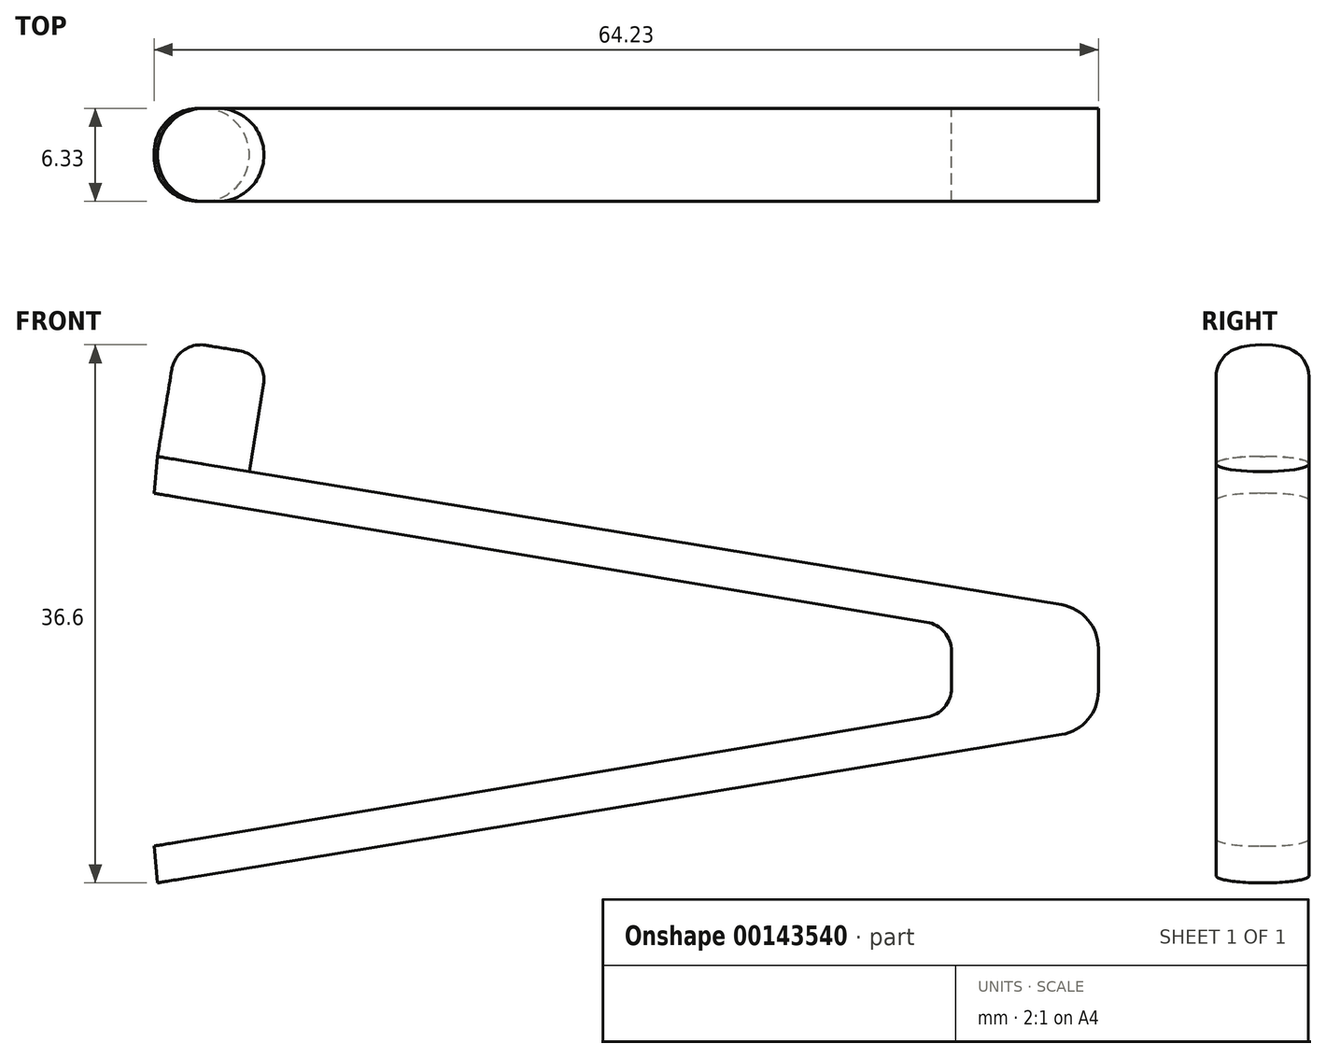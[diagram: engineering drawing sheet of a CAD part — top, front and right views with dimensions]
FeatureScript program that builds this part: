
annotation { "Feature Type Name" : "Feature", "Feature Type Description" : "" }
export const myFeature = defineFeature(function(context is Context, id is Id, definition is map)
    precondition{}
    {
        {
            var Q0;
            Q0=qCreatedBy(makeId("Front.planeOp"),FACE);
            var sketch = newSketch(context, id + "F0", { "sketchPlane" : qUnion([Q0])});
            skLineSegment(sketch, "E0", {"start": v(-30, 14.5) * mm, "end": v(34, 4) * mm});
            skLineSegment(sketch, "E1", {"start": v(34, 4) * mm, "end": v(34, -4) * mm});
            skLineSegment(sketch, "E2", {"start": v(34, -4) * mm, "end": v(-30, -14.5) * mm});
            skLineSegment(sketch, "E3.1", {"start": v(24, -2.96) * mm, "end": v(-30.23, -12) * mm});
            skLineSegment(sketch, "E3.2", {"start": v(-30.23, 12) * mm, "end": v(24, 2.96) * mm});
            skLineSegment(sketch, "E4", {"start": v(24, 2.96) * mm, "end": v(24, -2.96) * mm});
            skLineSegment(sketch, "E5", {"start": v(-30, 14.5) * mm, "end": v(-30.23, 12) * mm});
            skLineSegment(sketch, "E6", {"start": v(-30.23, -12) * mm, "end": v(-30, -14.5) * mm});
            skSolve(sketch);
        }
        {
            var Q0;
            Q0=makeQuery(id+"F0.imprint","IMPRINT",FACE,{"disambiguationData":[TD([[makeQuery(id+"F0.imprint","IMPRINT",EDGE,{"derivedFrom":sQuery(id+"F0.wireOp",EDGE,"E0")}),-1.0]])]});
            var Q1;
            Q1=sQuery(id+"F0.wireOp",EDGE,"9byXGtGL-TiKi-ESHT-9G8f-rp2WdieyN90J");
            var Q2;
            Q2=sQuery(id+"F0.wireOp",EDGE,"E1");
            var Q3;
            Q3=sQuery(id+"F0.wireOp",EDGE,"E3.0");
            var Q4;
            Q4=sQuery(id+"F0.wireOp",EDGE,"E2");
            var Q5;
            Q5=sQuery(id+"F0.wireOp",EDGE,"E3.1");
            var Q6;
            Q6=sQuery(id+"F0.wireOp",EDGE,"E3.2");
            var Q7;
            Q7=sQuery(id+"F0.wireOp",EDGE,"E3.3");
            var Q8;
            Q8=sQuery(id+"F0.wireOp",EDGE,"E0");
            var Q9;
            Q9=sQuery(id+"F0.wireOp",EDGE,"E4");
            var Q10;
            Q10=sQuery(id+"F0.wireOp",EDGE,"WK7Iqi4k-UJnr-hG7o-36dU-zjlxEIJufRnm");
            var Q11;
            Q11=sQuery(id+"F0.wireOp",EDGE,"wQO7SIwi-us3T-ShAA-4KbL-jPIoXWtiWfxA");
            var Q12;
            Q12=sQuery(id+"F0.wireOp",EDGE,"2IcxQzrb-WH7L-S9HZ-jIrS-pt4sDyhrxdYz");
            extrude(context, id + "F1", {"entities" : qUnion([Q0]), "surfaceEntities" : qUnion([Q1, Q2, Q3, Q4, Q5, Q6, Q7, Q8, Q9, Q10, Q11, Q12]), "depth" : 6.33 * mm});
        }
        {
            var Q0;
            Q0=makeQuery(id+"F1.opExtrude","SWEPT_EDGE",EDGE,{"disambiguationData":[OSD([sQuery(id+"F0.wireOp",EDGE,"E3.1"),sQuery(id+"F0.wireOp",EDGE,"E4")])]});
            var Q1;
            Q1=makeQuery(id+"F1.opExtrude","SWEPT_EDGE",EDGE,{"disambiguationData":[OSD([sQuery(id+"F0.wireOp",EDGE,"E3.2"),sQuery(id+"F0.wireOp",EDGE,"E4")])]});
            fillet(context, id + "F2", {"entities" : qUnion([Q0, Q1]), "radius" : 2 * mm, "tangentPropagation" : true, "allowEdgeOverflow" : false});
        }
        {
            var Q0;
            Q0=makeQuery(id+"F1.opExtrude","SWEPT_EDGE",EDGE,{"disambiguationData":[OSD([sQuery(id+"F0.wireOp",EDGE,"E0"),sQuery(id+"F0.wireOp",EDGE,"E1")])]});
            var Q1;
            Q1=makeQuery(id+"F1.opExtrude","SWEPT_EDGE",EDGE,{"disambiguationData":[OSD([sQuery(id+"F0.wireOp",EDGE,"E1"),sQuery(id+"F0.wireOp",EDGE,"E2")])]});
            fillet(context, id + "F3", {"entities" : qUnion([Q0, Q1]), "radius" : 3 * mm, "tangentPropagation" : true, "allowEdgeOverflow" : false});
        }
        {
            var Q0;
            Q0=makeQuery(id+"F1.opExtrude","SWEPT_FACE",FACE,{"disambiguationData":[OSD([sQuery(id+"F0.wireOp",EDGE,"E0")])]});
            var sketch = newSketch(context, id + "F4", { "sketchPlane" : qUnion([Q0])});
            skCircle(sketch, "E7", {"center": v(-28.79, -3.17) * mm, "radius": 3.17 * mm});
            skSolve(sketch);
        }
        {
            var Q0;
            {var subQ0=sQuery(id+"F4.wireOp",EDGE,"E7");var subQ1=sQuery(id+"F0.wireOp",EDGE,"E0");var subQ3=makeQuery(id+"F4.imprint","INTERSECT",VERTEX,{"derivedFrom":[makeQuery(id+"F1.opExtrude","CAP_EDGE",EDGE,{"disambiguationData":[OSD([subQ1])],"isStart":true}),subQ0]});Q0=makeQuery(id+"F4.imprint","IMPRINT",FACE,{"disambiguationData":[TD([[makeQuery(id+"F4.imprint","IMPRINT",EDGE,{"disambiguationData":[TD([[subQ3,1.0]])],"derivedFrom":subQ0}),1.0]])]});}
            extrude(context, id + "F5", {"entities" : qUnion([Q0]), "operationType" : NewBodyOperationType.ADD, "depth" : 8 * mm});
        }
        {
            var Q0;
            Q0=makeQuery(id+"F5.opExtrude","CAP_EDGE",EDGE,{"disambiguationData":[OSD([sQuery(id+"F4.wireOp",EDGE,"E7")])],"isStart":false});
            fillet(context, id + "F6", {"entities" : qUnion([Q0]), "radius" : 2 * mm, "tangentPropagation" : true, "allowEdgeOverflow" : false});
        }
        {
            var Q0;
            Q0=makeQuery(id+"F1.opExtrude","CAP_EDGE",EDGE,{"disambiguationData":[OSD([sQuery(id+"F0.wireOp",EDGE,"E5")])],"isStart":true});
            var Q1;
            Q1=makeQuery(id+"F1.opExtrude","CAP_EDGE",EDGE,{"disambiguationData":[OSD([sQuery(id+"F0.wireOp",EDGE,"E5")])],"isStart":false});
            var Q2;
            Q2=makeQuery(id+"F1.opExtrude","CAP_EDGE",EDGE,{"disambiguationData":[OSD([sQuery(id+"F0.wireOp",EDGE,"E6")])],"isStart":true});
            var Q3;
            Q3=makeQuery(id+"F1.opExtrude","CAP_EDGE",EDGE,{"disambiguationData":[OSD([sQuery(id+"F0.wireOp",EDGE,"E6")])],"isStart":false});
            fillet(context, id + "F7", {"entities" : qUnion([Q0, Q1, Q2, Q3]), "radius" : 3 * mm, "tangentPropagation" : true, "allowEdgeOverflow" : false});
        }
    });
